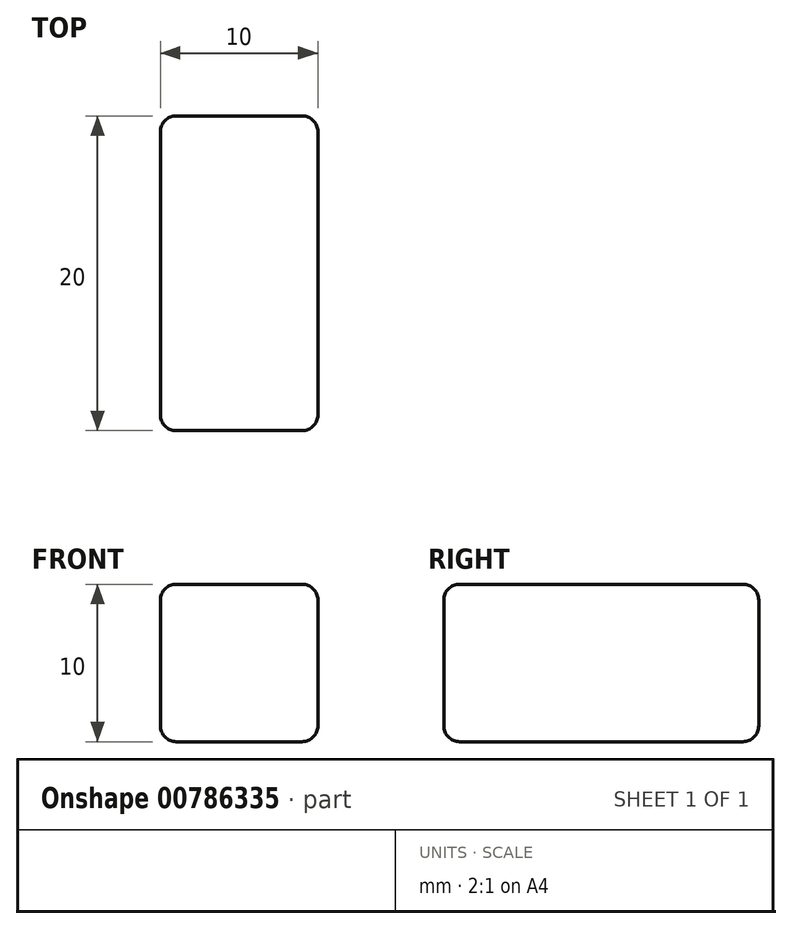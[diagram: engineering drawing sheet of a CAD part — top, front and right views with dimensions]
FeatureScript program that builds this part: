
annotation { "Feature Type Name" : "Feature", "Feature Type Description" : "" }
export const myFeature = defineFeature(function(context is Context, id is Id, definition is map)
    precondition{}
    {
        {
            var Q0;
            Q0=qCreatedBy(makeId("Front.planeOp"),FACE);
            var sketch = newSketch(context, id + "F0", { "sketchPlane" : qUnion([Q0])});
            skLineSegment(sketch, "E0.bottom", {"start": v(0, 0) * mm, "end": v(10, 0) * mm});
            skLineSegment(sketch, "E0.top", {"start": v(0, 10) * mm, "end": v(10, 10) * mm});
            skLineSegment(sketch, "E0.left", {"start": v(0, 0) * mm, "end": v(0, 10) * mm});
            skLineSegment(sketch, "E0.right", {"start": v(10, 0) * mm, "end": v(10, 10) * mm});
            skSolve(sketch);
        }
        {
            var Q0;
            Q0 = qSketchRegion(id + "F0", true);
            extrude(context, id + "F1", {"entities" : qUnion([Q0]), "depth" : 20 * mm, "offsetDistance" : 25 * mm});
        }
        {
            var Q0;
            Q0=makeQuery(id+"F1.opExtrude","CAP_FACE",FACE,{"disambiguationData":[OSD([sQuery(id+"F0.wireOp",EDGE,"E0.bottom"),sQuery(id+"F0.wireOp",EDGE,"E0.top"),sQuery(id+"F0.wireOp",EDGE,"E0.left"),sQuery(id+"F0.wireOp",EDGE,"E0.right")])],"isStart":false});
            var Q1;
            Q1=makeQuery(id+"F1.opExtrude","SWEPT_FACE",FACE,{"disambiguationData":[OSD([sQuery(id+"F0.wireOp",EDGE,"E0.right")])]});
            var Q2;
            Q2=makeQuery(id+"F1.opExtrude","CAP_FACE",FACE,{"disambiguationData":[OSD([sQuery(id+"F0.wireOp",EDGE,"E0.bottom"),sQuery(id+"F0.wireOp",EDGE,"E0.top"),sQuery(id+"F0.wireOp",EDGE,"E0.left"),sQuery(id+"F0.wireOp",EDGE,"E0.right")])],"isStart":true});
            var Q3;
            Q3=makeQuery(id+"F1.opExtrude","SWEPT_FACE",FACE,{"disambiguationData":[OSD([sQuery(id+"F0.wireOp",EDGE,"E0.left")])]});
            var Q4;
            Q4=makeQuery(id+"F1.opExtrude","SWEPT_FACE",FACE,{"disambiguationData":[OSD([sQuery(id+"F0.wireOp",EDGE,"E0.top")])]});
            fillet(context, id + "F2", {"entities" : qUnion([Q0, Q1, Q2, Q3, Q4]), "radius" : 1 * mm, "tangentPropagation" : true, "allowEdgeOverflow" : false});
        }
    });
